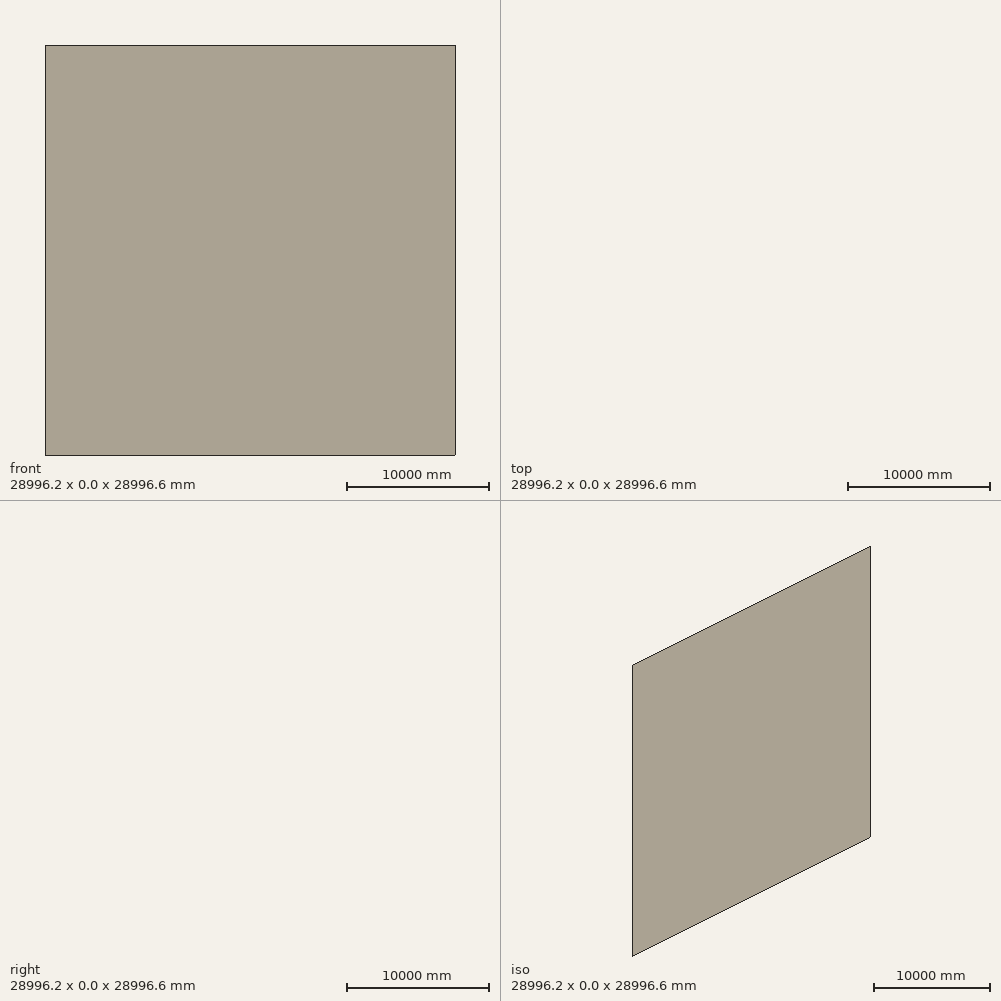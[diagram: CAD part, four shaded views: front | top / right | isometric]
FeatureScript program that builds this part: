
annotation { "Feature Type Name" : "Feature", "Feature Type Description" : "" }
export const myFeature = defineFeature(function(context is Context, id is Id, definition is map)
    precondition{}
    {
        {
            var Q0;
            Q0=qCreatedBy(makeId("Top.planeOp"),FACE);
            var sketch = newSketch(context, id + "F0", { "sketchPlane" : qUnion([Q0])});
            skLineSegment(sketch, "E0", {"start": v(0, 0) * mm, "end": v(-329955.68, 190500) * mm, "construction": true});
            skLineSegment(sketch, "E1", {"start": v(-329955.68, 10160) * mm, "end": v(0, 10160) * mm, "construction": true});
            skLineSegment(sketch, "E2", {"start": v(-329955.68, 190500) * mm, "end": v(-14782.4, 0) * mm});
            skLineSegment(sketch, "E3", {"start": v(-329955.68, 190500) * mm, "end": v(15847.37, 0) * mm});
            skLineSegment(sketch, "E4", {"start": v(-31591.64, 10160) * mm, "end": v(-2595.46, 10160) * mm});
            skLineSegment(sketch, "E5", {"start": v(0, 0) * mm, "end": v(0, 190500) * mm, "construction": true});
            skSolve(sketch);
        }
        {
            var Q0;
            Q0=sQuery(id+"F0.wireOp",EDGE,"E4");
            extrude(context, id + "F1", {"bodyType" : ToolBodyType.SURFACE, "surfaceEntities" : qUnion([Q0]), "depth" : 14498.32 * mm, "offsetDistance" : 25.4 * mm, "hasSecondDirection" : true, "secondDirectionOppositeDirection" : true, "secondDirectionDepth" : 14498.32 * mm});
        }
    });
